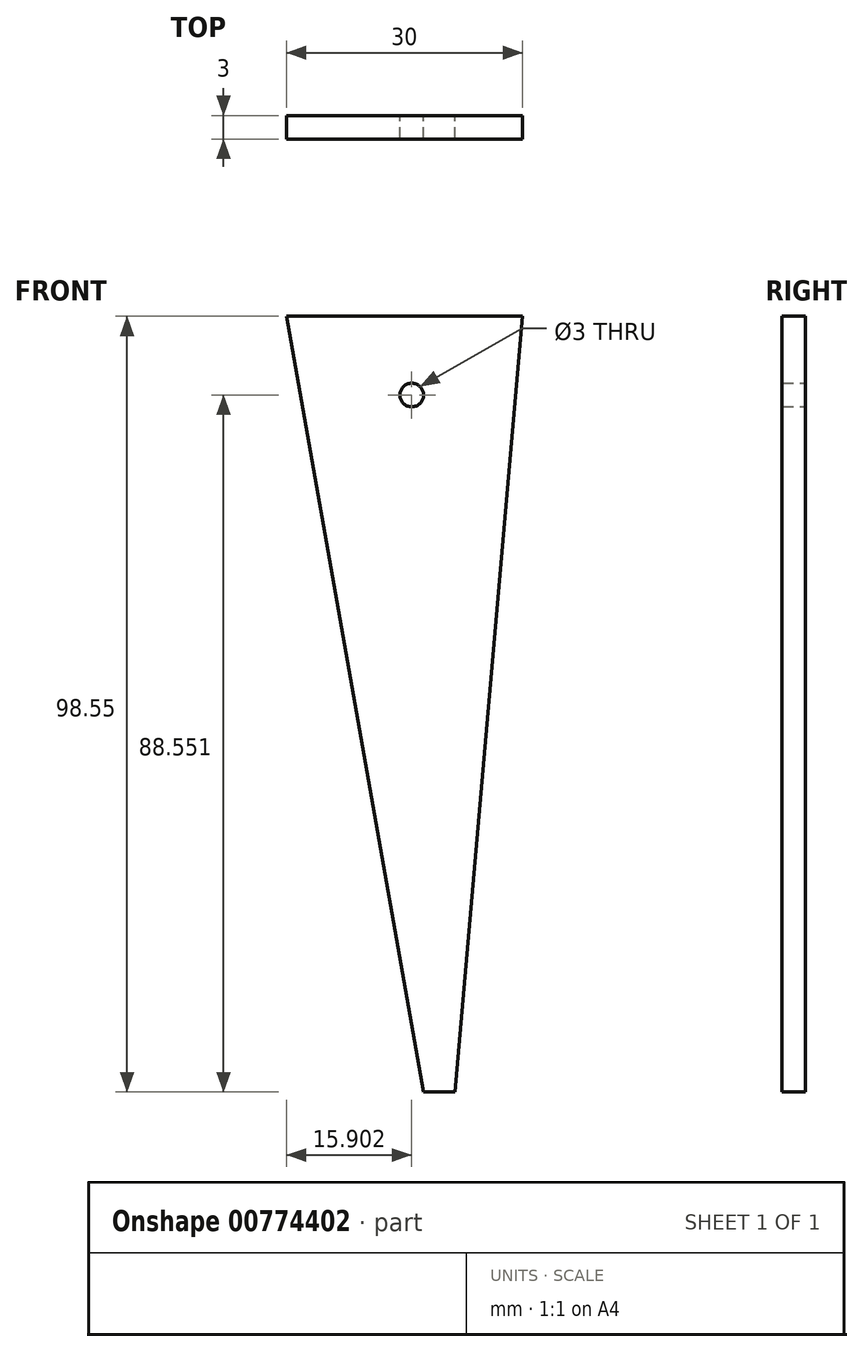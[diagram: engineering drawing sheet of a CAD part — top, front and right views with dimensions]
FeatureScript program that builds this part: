
annotation { "Feature Type Name" : "Feature", "Feature Type Description" : "" }
export const myFeature = defineFeature(function(context is Context, id is Id, definition is map)
    precondition{}
    {
        {
            var Q0;
            Q0=qCreatedBy(makeId("Front.planeOp"),FACE);
            var sketch = newSketch(context, id + "F0", { "sketchPlane" : qUnion([Q0])});
            skLineSegment(sketch, "E0", {"start": v(-20.7, 19.2) * mm, "end": v(9.3, 19.2) * mm});
            skLineSegment(sketch, "E1", {"start": v(9.3, 19.2) * mm, "end": v(0.68, -79.36) * mm});
            skLineSegment(sketch, "E2", {"start": v(0.68, -79.36) * mm, "end": v(-3.32, -79.36) * mm});
            skLineSegment(sketch, "E3", {"start": v(-3.32, -79.36) * mm, "end": v(-20.7, 19.2) * mm});
            skSolve(sketch);
        }
        {
            var Q0;
            Q0 = qSketchRegion(id + "F0", true);
            extrude(context, id + "F1", {"entities" : qUnion([Q0]), "depth" : 3 * mm, "offsetDistance" : 25 * mm, "symmetric" : true});
        }
        {
            var Q0;
            Q0=makeQuery(id+"F1.opExtrude","CAP_FACE",FACE,{"disambiguationData":[OSD([sQuery(id+"F0.wireOp",EDGE,"E0"),sQuery(id+"F0.wireOp",EDGE,"E1"),sQuery(id+"F0.wireOp",EDGE,"E2"),sQuery(id+"F0.wireOp",EDGE,"E3")])],"isStart":true});
            var sketch = newSketch(context, id + "F2", { "sketchPlane" : qUnion([Q0])});
            skPoint(sketch, "E4", {"position": v(4.79, 9.2) * mm});
            skCircle(sketch, "E5", {"center": v(4.79, 9.2) * mm, "radius": 1.5 * mm});
            skSolve(sketch);
        }
        {
            var Q0;
            Q0=makeQuery(id+"F2.imprint","IMPRINT",FACE,{"disambiguationData":[TD([[makeQuery(id+"F2.imprint","IMPRINT",EDGE,{"derivedFrom":sQuery(id+"F2.wireOp",EDGE,"E5")}),1.0]])]});
            extrude(context, id + "F3", {"entities" : qUnion([Q0]), "operationType" : NewBodyOperationType.REMOVE, "endBound" : BoundingType.THROUGH_ALL, "oppositeDirection" : true, "depth" : 25 * mm, "offsetDistance" : 25 * mm});
        }
    });
